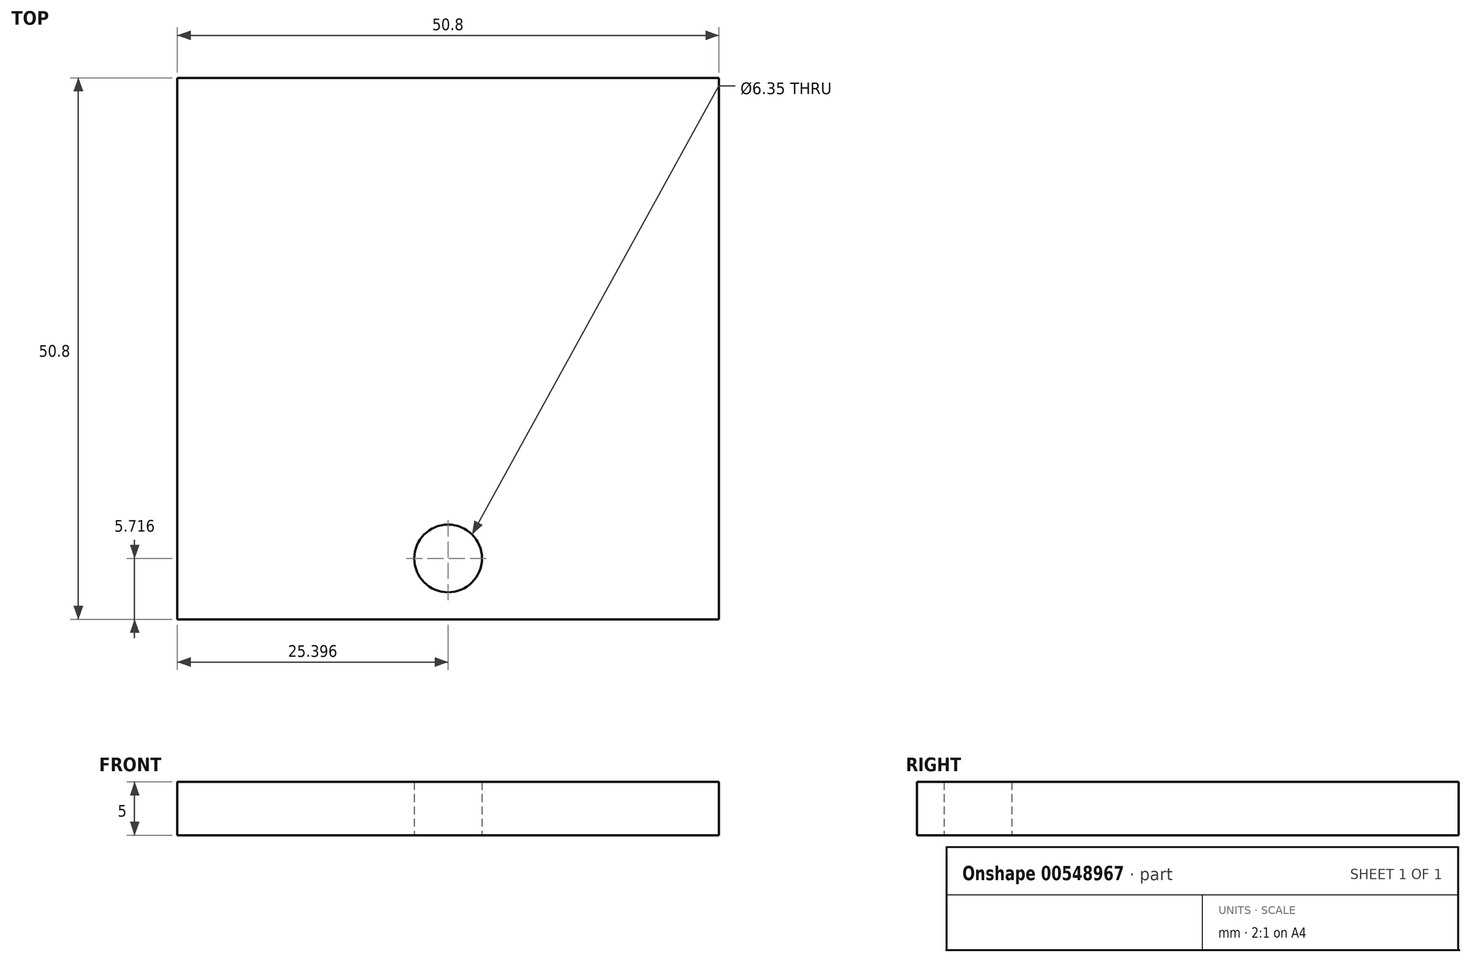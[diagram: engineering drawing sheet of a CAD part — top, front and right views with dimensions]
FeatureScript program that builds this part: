
annotation { "Feature Type Name" : "Feature", "Feature Type Description" : "" }
export const myFeature = defineFeature(function(context is Context, id is Id, definition is map)
    precondition{}
    {
        {
            var Q0;
            Q0=qCreatedBy(makeId("Top.planeOp"),FACE);
            var sketch = newSketch(context, id + "F0", { "sketchPlane" : qUnion([Q0])});
            skLineSegment(sketch, "E0.bottom", {"start": v(-14.11, -14.22) * mm, "end": v(36.69, -14.22) * mm});
            skLineSegment(sketch, "E0.top", {"start": v(-14.11, 36.58) * mm, "end": v(36.69, 36.58) * mm});
            skLineSegment(sketch, "E0.left", {"start": v(-14.11, -14.22) * mm, "end": v(-14.11, 36.58) * mm});
            skLineSegment(sketch, "E0.right", {"start": v(36.69, -14.22) * mm, "end": v(36.69, 36.58) * mm});
            skCircle(sketch, "E1", {"center": v(11.29, -8.5) * mm, "radius": 3.18 * mm});
            skPoint(sketch, "E1.centerSnap0", {"position": v(11.29, -14.22) * mm});
            skSolve(sketch);
        }
        {
            var Q0;
            Q0=makeQuery(id+"F0.imprint","IMPRINT",FACE,{"disambiguationData":[TD([[makeQuery(id+"F0.imprint","IMPRINT",EDGE,{"derivedFrom":sQuery(id+"F0.wireOp",EDGE,"E0.bottom")}),1.0]])]});
            extrude(context, id + "F1", {"entities" : qUnion([Q0]), "depth" : 5 * mm, "offsetDistance" : 25.4 * mm});
        }
    });
